# Revit family: Plumbing-Fix_Flush-Valve-Touchless_Stern_Nara
name_source: partatom
category: Plumbing Fixtures
revit_build: Autodesk Revit 2018 (Build: 20170927_1515(x64)
units: mm (PartAtom-declared; Revit-internal decimal feet)

## family parameters
Cut with Voids When Loaded = No
Host = Face
OmniClass Number = 23.45.05.14
OmniClass Title = Plumbing Fixtures - Sanitary Washing Units
Part Type = Normal
Room Calculation Point = No
Round Connector Dimension = Use Diameter
Shared = No

## types (2) — shared parameters
Assembly Code = D2010300
Available Options = as Specified
Body Construction = Brass
CW Connection = Yes
CWFU = 1
Default Elevation = 0' - 0"
GPF = 1.58
HW Connection = No
Manufacturer = Stern Engineering
Manufacturer Website = http://www.sternfaucets.com
Operating Pressure Range = 7.26 - 116 PSI  ;  0.5 - 8 bar
Operating Temperature Range = as Specified
Piping_Flow = 0 GPM
Piping_Inlet Diameter = 1"
Product Data = http://www.arcat.com
Product Features = Dual Flush  ;  0.79 or 1.18 or 1.58 GPF  ;  24 Hr Auto Flush
Revision = R1_2018-04
Sales Information = http://www.sternfaucets.com
Standards Conformance = as Specified
Type Comments = as Specified
URL = http://www.sternfaucets.com
Unit Height = 0' - 10 1/4"
Unit Width = 0' - 7 1/8"
Vent Connection = No
Warranty Duration (Years) = 2
Waste Connection = No
zero-valued in all types: Cost, Expected Lifespan (Years), HWFU, Maintenance Schedule (Months), WFU

## per-type parameters (varying)
| type | Description | Model | Power Supply |
| Battery Pack | Stern Touchless Flush Valve - Nara 3002 as Specified | Nara 3002 | 9V Battery |
| Transformer | Stern Touchless Flush Valve - Nara 3002 E as Specified | Nara 3002 E | 9V Transformer |

## geometry (parser evidence)
native form markers: Sweep x2
no freeform markers — native parametric forms only
